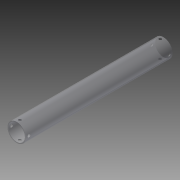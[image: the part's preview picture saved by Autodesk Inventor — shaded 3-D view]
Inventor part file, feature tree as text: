
AUTODESK INVENTOR PART (.ipt)
format: ipt  version: 2014 (Build 180170000, 170)  size: 148,992 bytes
history: native  units: in
note: dims shown in document units (in); Inventor stores cm internally (conversion verified against a paired STEP export)
features: extrude x3, sketch x3, plane x2, projected_geometry x1
ambient origin geometry x8: Origin, YZ Plane, XZ Plane, XY Plane, X Axis, Y Axis, Z Axis, Center Point
bodies: Solid1 (feature_tree)
feature tree (9):
  extrude  "Extrusion1"  Depth=1.125in
  plane  "Work Plane1"
  extrude  "Extrusion2"  Depth=5.0in
  plane  "Work Plane2"
  extrude  "Extrusion3"  Depth=0.2188in
  sketch  "Sketch1"  dims[d0=1.25in d1=1.125in]
  sketch  "Sketch2"  dims[d2=10.0in d3=0.0in d4=5.0in]
  projected_geometry  "Projected Loop1"
  sketch  "Sketch3"  dims[d5=0.19in d6=0.2188in d7=0.625in d8=2.0in d9=0.0in d10=5.0in d11=0.19in d12=0.2188in d13=0.625in d14=2.0in d15=0.0in]
